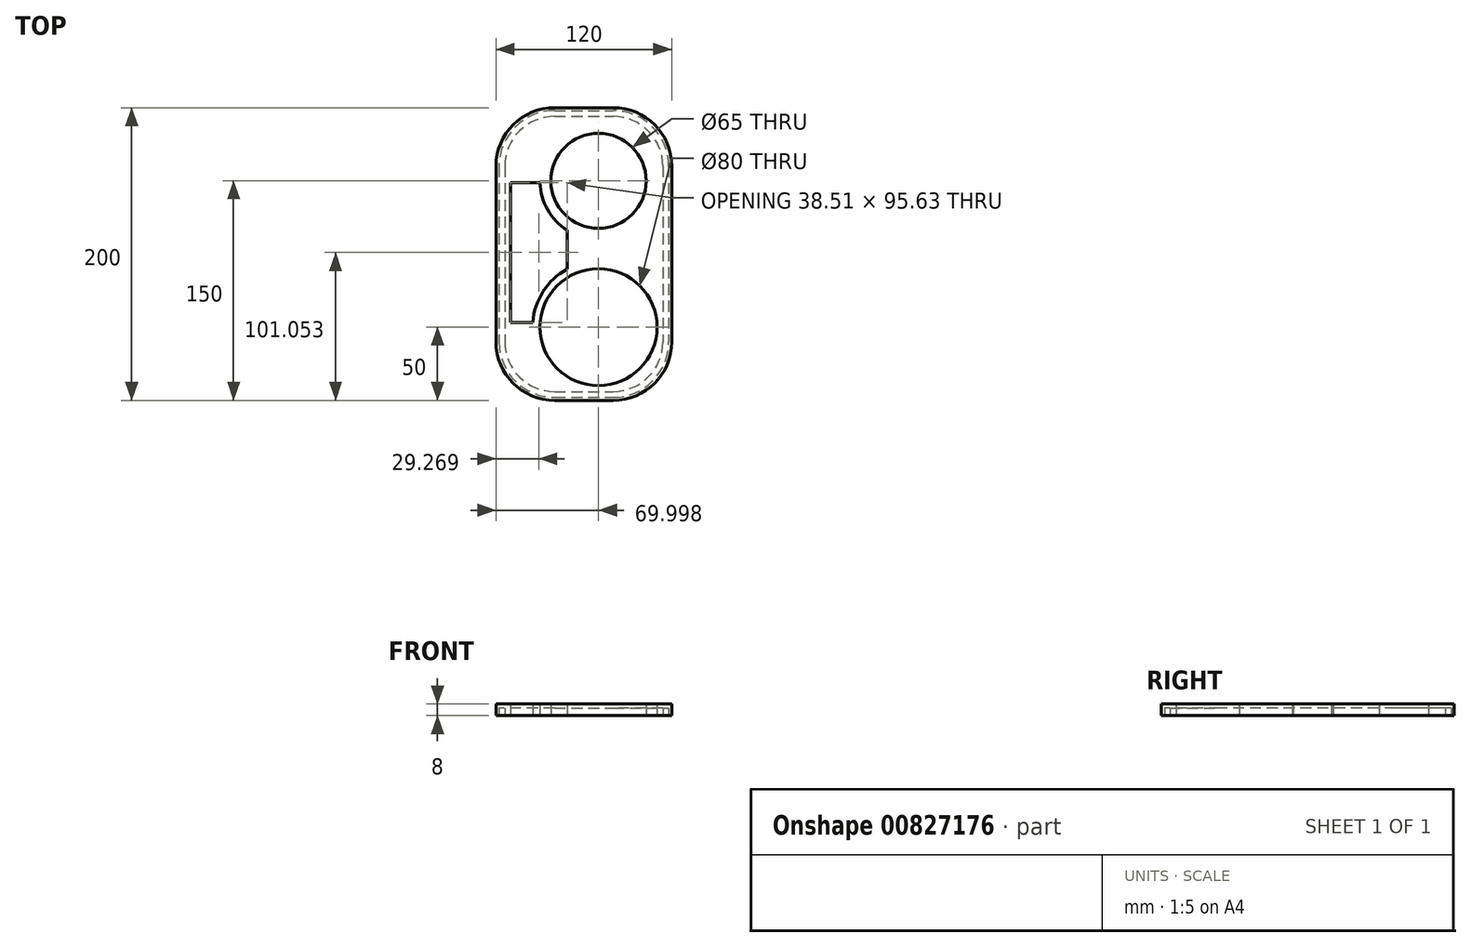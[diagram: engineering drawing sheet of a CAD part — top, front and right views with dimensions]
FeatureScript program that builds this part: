
annotation { "Feature Type Name" : "Feature", "Feature Type Description" : "" }
export const myFeature = defineFeature(function(context is Context, id is Id, definition is map)
    precondition{}
    {
        {
            var Q0;
            Q0=qCreatedBy(makeId("Top.planeOp"),FACE);
            var sketch = newSketch(context, id + "F0", { "sketchPlane" : qUnion([Q0])});
            skLineSegment(sketch, "E0.bottom", {"start": v(-30.11, 113.52) * mm, "end": v(9.89, 113.52) * mm});
            skLineSegment(sketch, "E0.top", {"start": v(-30.11, -86.48) * mm, "end": v(9.89, -86.48) * mm});
            skLineSegment(sketch, "E0.left", {"start": v(-70.11, 73.52) * mm, "end": v(-70.11, -46.48) * mm});
            skLineSegment(sketch, "E0.right", {"start": v(49.89, 73.52) * mm, "end": v(49.89, -46.48) * mm});
            skPoint(sketch, "E1.visualSharp", {"position": v(-70.11, 113.52) * mm});
            skArc(sketch, "E1.filletArc", {"start": v(-30.11, 113.52) * mm, "mid": v(-58.4, 101.8) * mm, "end": v(-70.11, 73.52) * mm});
            skPoint(sketch, "E2.visualSharp", {"position": v(49.89, 113.52) * mm});
            skArc(sketch, "E2.filletArc", {"start": v(49.89, 73.52) * mm, "mid": v(38.17, 101.8) * mm, "end": v(9.89, 113.52) * mm});
            skPoint(sketch, "E3.visualSharp", {"position": v(-70.11, -86.48) * mm});
            skArc(sketch, "E3.filletArc", {"start": v(-70.11, -46.48) * mm, "mid": v(-58.4, -74.76) * mm, "end": v(-30.11, -86.48) * mm});
            skPoint(sketch, "E4.visualSharp", {"position": v(49.89, -86.48) * mm});
            skArc(sketch, "E4.filletArc", {"start": v(9.89, -86.48) * mm, "mid": v(38.17, -74.76) * mm, "end": v(49.89, -46.48) * mm});
            skLineSegment(sketch, "E5", {"start": v(9.89, -86.48) * mm, "end": v(-0.11, -86.48) * mm, "construction": true});
            skLineSegment(sketch, "E6", {"start": v(-0.11, -86.48) * mm, "end": v(-0.11, -36.48) * mm, "construction": true});
            skLineSegment(sketch, "E7", {"start": v(9.89, 113.52) * mm, "end": v(-0.11, 113.52) * mm, "construction": true});
            skLineSegment(sketch, "E8", {"start": v(-0.11, 113.52) * mm, "end": v(-0.11, 63.52) * mm, "construction": true});
            skCircle(sketch, "E9", {"center": v(-0.11, 63.52) * mm, "radius": 32.5 * mm});
            skCircle(sketch, "E10", {"center": v(-0.11, -36.48) * mm, "radius": 40 * mm});
            skArc(sketch, "E11.0", {"start": v(-30.11, 111.52) * mm, "mid": v(-56.98, 100.39) * mm, "end": v(-68.11, 73.52) * mm});
            skLineSegment(sketch, "E11.1", {"start": v(-30.11, 111.52) * mm, "end": v(9.89, 111.52) * mm});
            skLineSegment(sketch, "E11.2", {"start": v(-68.11, 73.52) * mm, "end": v(-68.11, -46.48) * mm});
            skArc(sketch, "E11.3", {"start": v(47.89, 73.52) * mm, "mid": v(36.76, 100.39) * mm, "end": v(9.89, 111.52) * mm});
            skArc(sketch, "E11.4", {"start": v(-68.11, -46.48) * mm, "mid": v(-56.98, -73.35) * mm, "end": v(-30.11, -84.48) * mm});
            skLineSegment(sketch, "E11.5", {"start": v(-30.11, -84.48) * mm, "end": v(9.89, -84.48) * mm});
            skArc(sketch, "E11.6", {"start": v(9.89, -84.48) * mm, "mid": v(36.76, -73.35) * mm, "end": v(47.89, -46.48) * mm});
            skLineSegment(sketch, "E11.7", {"start": v(47.89, 73.52) * mm, "end": v(47.89, -46.48) * mm});
            skLineSegment(sketch, "E12.0", {"start": v(-64.11, 73.52) * mm, "end": v(-64.11, -46.48) * mm});
            skArc(sketch, "E12.1", {"start": v(-30.11, 107.52) * mm, "mid": v(-54.15, 97.56) * mm, "end": v(-64.11, 73.52) * mm});
            skArc(sketch, "E12.2", {"start": v(-64.11, -46.48) * mm, "mid": v(-54.15, -70.52) * mm, "end": v(-30.11, -80.48) * mm});
            skLineSegment(sketch, "E12.3", {"start": v(-30.11, 107.52) * mm, "end": v(9.89, 107.52) * mm});
            skLineSegment(sketch, "E12.4", {"start": v(-30.11, -80.48) * mm, "end": v(9.89, -80.48) * mm});
            skArc(sketch, "E12.5", {"start": v(9.89, -80.48) * mm, "mid": v(33.93, -70.52) * mm, "end": v(43.89, -46.48) * mm});
            skLineSegment(sketch, "E12.6", {"start": v(43.89, 73.52) * mm, "end": v(43.89, -46.48) * mm});
            skArc(sketch, "E12.7", {"start": v(43.89, 73.52) * mm, "mid": v(33.93, 97.56) * mm, "end": v(9.89, 107.52) * mm});
            skArc(sketch, "E13", {"start": v(-40.1, 62.4) * mm, "mid": v(-34.9, 43.78) * mm, "end": v(-21.59, 29.77) * mm});
            skArc(sketch, "E14", {"start": v(-21.59, 3.07) * mm, "mid": v(-37.93, -12.1) * mm, "end": v(-45, -33.24) * mm});
            skLineSegment(sketch, "E15", {"start": v(-21.59, 29.77) * mm, "end": v(-21.59, 3.07) * mm});
            skLineSegment(sketch, "E16", {"start": v(-40.1, 62.4) * mm, "end": v(-60.1, 62.4) * mm});
            skLineSegment(sketch, "E17", {"start": v(-60.1, 62.4) * mm, "end": v(-60.1, -33.24) * mm});
            skLineSegment(sketch, "E18", {"start": v(-45, -33.24) * mm, "end": v(-60.1, -33.24) * mm});
            skLineSegment(sketch, "E19.0", {"start": v(-42, 60.4) * mm, "end": v(-58.1, 60.4) * mm});
            skLineSegment(sketch, "E19.1", {"start": v(-23.59, 28.7) * mm, "end": v(-23.59, 4.24) * mm});
            skArc(sketch, "E19.2", {"start": v(-23.59, 4.24) * mm, "mid": v(-39.43, -10.73) * mm, "end": v(-46.82, -31.24) * mm});
            skArc(sketch, "E19.3", {"start": v(-42, 60.4) * mm, "mid": v(-36.43, 42.43) * mm, "end": v(-23.59, 28.7) * mm});
            skLineSegment(sketch, "E19.4", {"start": v(-46.82, -31.24) * mm, "end": v(-58.1, -31.24) * mm});
            skLineSegment(sketch, "E19.5", {"start": v(-58.1, 60.4) * mm, "end": v(-58.1, -31.24) * mm});
            skSolve(sketch);
        }
        {
            var Q0;
            Q0=makeQuery(id+"F0.imprint","IMPRINT",FACE,{"disambiguationData":[TD([[makeQuery(id+"F0.imprint","IMPRINT",EDGE,{"derivedFrom":sQuery(id+"F0.wireOp",EDGE,"E0.bottom")}),-1.0]])]});
            var Q1;
            Q1=makeQuery(id+"F0.imprint","IMPRINT",FACE,{"disambiguationData":[TD([[makeQuery(id+"F0.imprint","IMPRINT",EDGE,{"derivedFrom":sQuery(id+"F0.wireOp",EDGE,"E11.0")}),1.0]])]});
            var Q2;
            Q2=makeQuery(id+"F0.imprint","IMPRINT",FACE,{"disambiguationData":[TD([[makeQuery(id+"F0.imprint","IMPRINT",EDGE,{"derivedFrom":sQuery(id+"F0.wireOp",EDGE,"E9")}),-1.0]])]});
            extrude(context, id + "F1", {"entities" : qUnion([Q0, Q1, Q2]), "depth" : 8 * mm, "offsetDistance" : 25 * mm});
        }
        {
            var Q0;
            Q0=makeQuery(id+"F0.imprint","IMPRINT",FACE,{"disambiguationData":[TD([[makeQuery(id+"F0.imprint","IMPRINT",EDGE,{"derivedFrom":sQuery(id+"F0.wireOp",EDGE,"E11.0")}),1.0]])]});
            extrude(context, id + "F2", {"entities" : qUnion([Q0]), "operationType" : NewBodyOperationType.REMOVE, "depth" : 5 * mm, "offsetDistance" : 25 * mm});
        }
    });
